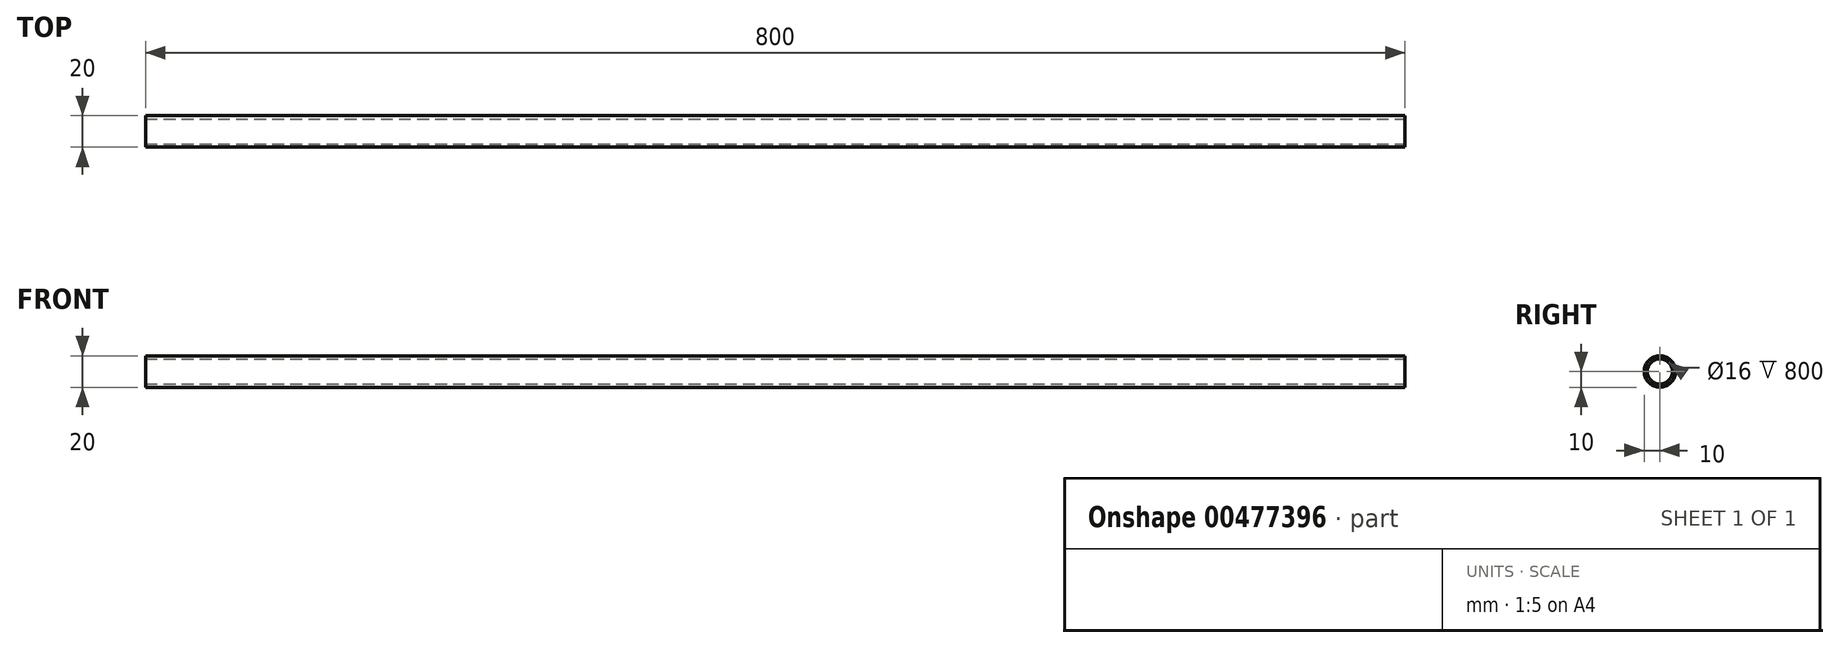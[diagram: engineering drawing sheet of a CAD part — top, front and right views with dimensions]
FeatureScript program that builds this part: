
annotation { "Feature Type Name" : "Feature", "Feature Type Description" : "" }
export const myFeature = defineFeature(function(context is Context, id is Id, definition is map)
    precondition{}
    {
        {
            var Q0;
            Q0=qCreatedBy(makeId("Top.planeOp"),FACE);
            var sketch = newSketch(context, id + "F0", { "sketchPlane" : qUnion([Q0])});
            skLineSegment(sketch, "E0", {"start": v(-342.86, 0) * mm, "end": v(457.14, 0) * mm});
            skSolve(sketch);
        }
        {
            var Q0;
            Q0=qCreatedBy(makeId("Right.planeOp"),FACE);
            var sketch = newSketch(context, id + "F1", { "sketchPlane" : qUnion([Q0])});
            skCircle(sketch, "E1", {"center": v(0, 0) * mm, "radius": 10 * mm});
            skCircle(sketch, "E2", {"center": v(0, 0) * mm, "radius": 8 * mm});
            skSolve(sketch);
        }
        {
            var Q0;
            Q0=makeQuery(id+"F1.imprint","IMPRINT",FACE,{"disambiguationData":[TD([[makeQuery(id+"F1.imprint","IMPRINT",EDGE,{"derivedFrom":sQuery(id+"F1.wireOp",EDGE,"E1")}),1.0]])]});
            var Q1;
            Q1=sQuery(id+"F0.wireOp",EDGE,"E0");
            sweep(context, id + "F2", {"profiles" : qUnion([Q0]), "path" : qUnion([Q1])});
        }
    });
